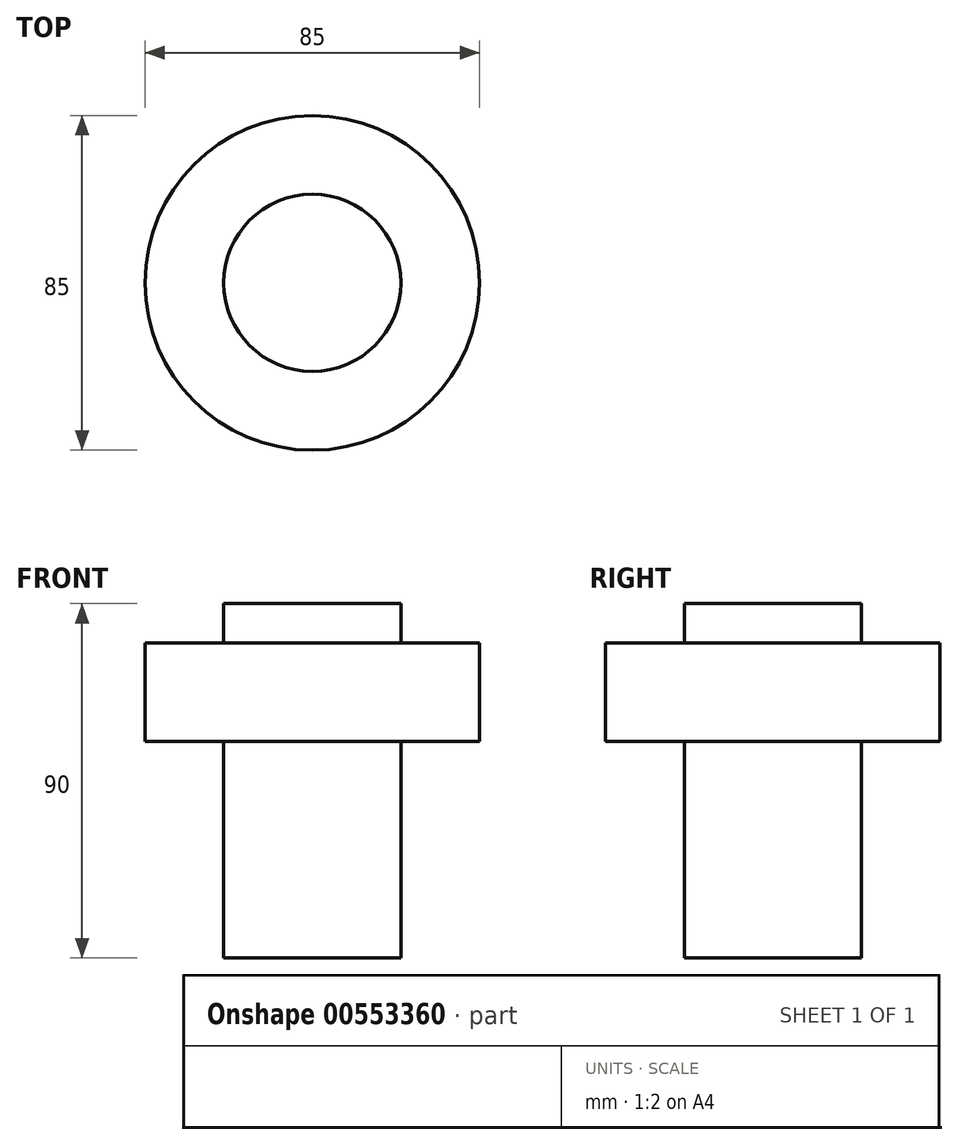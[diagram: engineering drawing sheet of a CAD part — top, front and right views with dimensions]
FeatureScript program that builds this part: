
annotation { "Feature Type Name" : "Feature", "Feature Type Description" : "" }
export const myFeature = defineFeature(function(context is Context, id is Id, definition is map)
    precondition{}
    {
        {
            var Q0;
            Q0=qCreatedBy(makeId("Top.planeOp"),FACE);
            var sketch = newSketch(context, id + "F0", { "sketchPlane" : qUnion([Q0])});
            skCircle(sketch, "E0", {"center": v(0, 0) * mm, "radius": 42.5 * mm});
            skSolve(sketch);
        }
        {
            var Q0;
            Q0=makeQuery(id+"F0.imprint","IMPRINT",FACE,{"disambiguationData":[TD([[makeQuery(id+"F0.imprint","IMPRINT",EDGE,{"derivedFrom":sQuery(id+"F0.wireOp",EDGE,"E0")}),1.0]])]});
            extrude(context, id + "F1", {"entities" : qUnion([Q0]), "depth" : 25 * mm, "offsetDistance" : 25 * mm});
        }
        {
            var Q0;
            Q0=makeQuery(id+"F1.opExtrude","CAP_FACE",FACE,{"disambiguationData":[OSD([sQuery(id+"F0.wireOp",EDGE,"E0")])],"isStart":false});
            var sketch = newSketch(context, id + "F2", { "sketchPlane" : qUnion([Q0])});
            skCircle(sketch, "E1", {"center": v(0, 0) * mm, "radius": 22.5 * mm});
            skSolve(sketch);
        }
        {
            var Q0;
            Q0=makeQuery(id+"F2.imprint","IMPRINT",FACE,{"disambiguationData":[TD([[makeQuery(id+"F2.imprint","IMPRINT",EDGE,{"derivedFrom":sQuery(id+"F2.wireOp",EDGE,"E1")}),1.0]])]});
            extrude(context, id + "F3", {"entities" : qUnion([Q0]), "operationType" : NewBodyOperationType.ADD, "depth" : 10 * mm, "offsetDistance" : 25 * mm, "hasSecondDirection" : true, "secondDirectionOppositeDirection" : true, "secondDirectionDepth" : 80 * mm});
        }
    });
